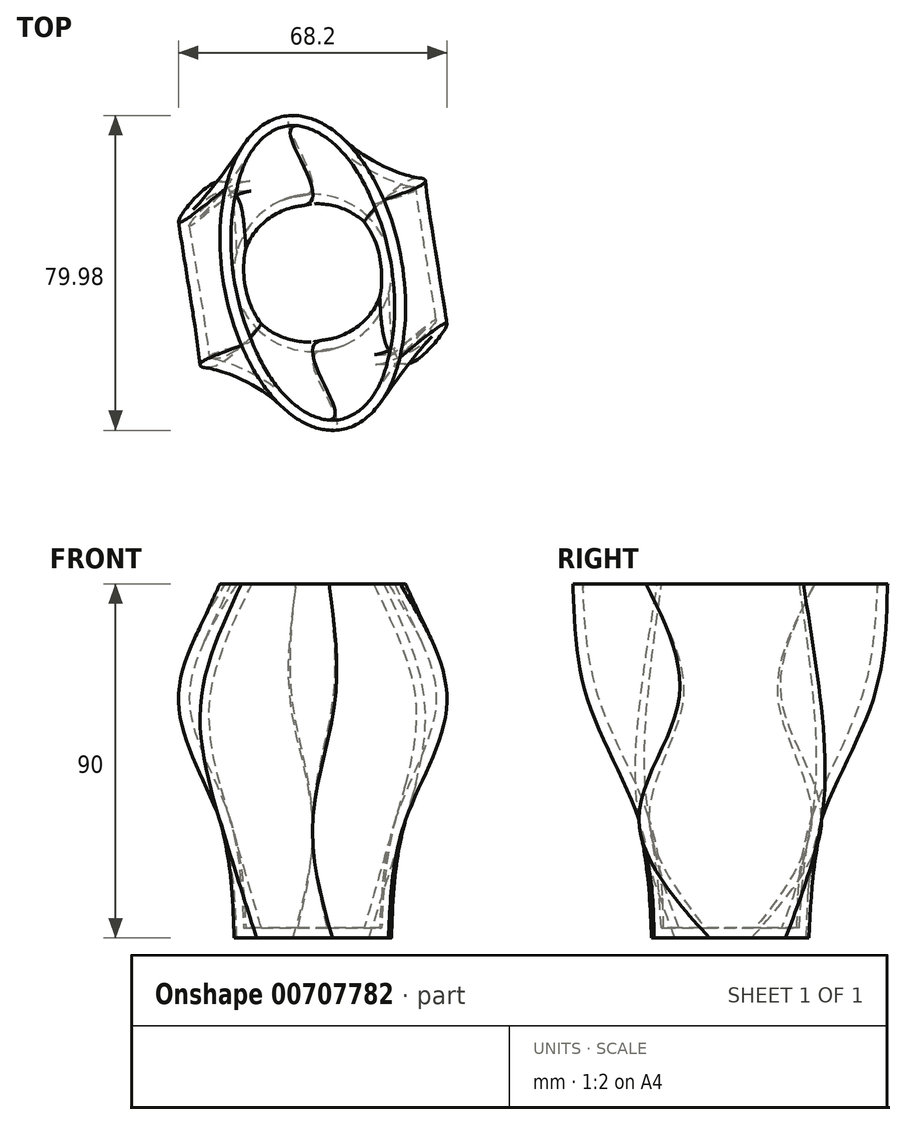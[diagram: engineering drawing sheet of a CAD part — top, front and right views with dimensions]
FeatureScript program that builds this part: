
annotation { "Feature Type Name" : "Feature", "Feature Type Description" : "" }
export const myFeature = defineFeature(function(context is Context, id is Id, definition is map)
    precondition{}
    {
        {
            var Q0;
            Q0=qCreatedBy(makeId("Top.planeOp"),FACE);
            cPlane(context, id + "F0", {"entities" : qUnion([Q0]), "cplaneType" : CPlaneType.OFFSET, "offset" : 30 * mm, "width" : 152.4 * mm, "height" : 152.4 * mm});
        }
        {
            var Q0;
            Q0=qCreatedBy(id+"F0.planeOp",FACE);
            cPlane(context, id + "F1", {"entities" : qUnion([Q0]), "cplaneType" : CPlaneType.OFFSET, "offset" : 30 * mm, "width" : 152.4 * mm, "height" : 152.4 * mm});
        }
        {
            var Q0;
            Q0=qCreatedBy(id+"F1.planeOp",FACE);
            cPlane(context, id + "F2", {"entities" : qUnion([Q0]), "cplaneType" : CPlaneType.OFFSET, "offset" : 30 * mm, "width" : 152.4 * mm, "height" : 152.4 * mm});
        }
        {
            var Q0;
            Q0=qCreatedBy(makeId("Top.planeOp"),FACE);
            var sketch = newSketch(context, id + "F3", { "sketchPlane" : qUnion([Q0])});
            skCircle(sketch, "E0", {"center": v(0, 0) * mm, "radius": 20 * mm});
            skSolve(sketch);
        }
        {
            var Q0;
            Q0=qCreatedBy(id+"F0.planeOp",FACE);
            var sketch = newSketch(context, id + "F4", { "sketchPlane" : qUnion([Q0])});
            skLineSegment(sketch, "E1.bottom", {"start": v(-23.6, -23.18) * mm, "end": v(23.6, -23.18) * mm});
            skLineSegment(sketch, "E1.top", {"start": v(-23.6, 23.18) * mm, "end": v(23.6, 23.18) * mm});
            skLineSegment(sketch, "E1.left", {"start": v(-23.6, -23.18) * mm, "end": v(-23.6, 23.18) * mm});
            skLineSegment(sketch, "E1.right", {"start": v(23.6, -23.18) * mm, "end": v(23.6, 23.18) * mm});
            skPoint(sketch, "E1.middle", {"position": v(0, 0) * mm});
            skSolve(sketch);
        }
        {
            var Q0;
            Q0=qCreatedBy(id+"F1.planeOp",FACE);
            var sketch = newSketch(context, id + "F5", { "sketchPlane" : qUnion([Q0])});
            skCircle(sketch, "E2.cCircle", {"center": v(0, 0) * mm, "radius": 31.65 * mm, "construction": true});
            skLineSegment(sketch, "E2.0", {"start": v(-28.44, -22.94) * mm, "end": v(-34.09, 13.16) * mm});
            skLineSegment(sketch, "E2.1", {"start": v(-34.09, 13.16) * mm, "end": v(-5.65, 36.1) * mm});
            skLineSegment(sketch, "E2.2", {"start": v(-5.65, 36.1) * mm, "end": v(28.44, 22.94) * mm});
            skLineSegment(sketch, "E2.3", {"start": v(28.44, 22.94) * mm, "end": v(34.09, -13.16) * mm});
            skLineSegment(sketch, "E2.4", {"start": v(34.09, -13.16) * mm, "end": v(5.65, -36.1) * mm});
            skLineSegment(sketch, "E2.5", {"start": v(5.65, -36.1) * mm, "end": v(-28.44, -22.94) * mm});
            skPoint(sketch, "E2.0.midPoint", {"position": v(-31.27, -4.9) * mm});
            skSolve(sketch);
        }
        {
            var Q0;
            Q0=qCreatedBy(id+"F2.planeOp",FACE);
            var sketch = newSketch(context, id + "F6", { "sketchPlane" : qUnion([Q0])});
            skEllipse(sketch, "E3", {"center": v(0, 0) * mm, "majorRadius": 40.46 * mm, "minorRadius": 22.76 * mm, "majorAxis": v(-0.18, 0.98)});
            skSolve(sketch);
        }
        {
            var Q0;
            Q0=makeQuery(id+"F3.imprint","IMPRINT",FACE,{"disambiguationData":[TD([[makeQuery(id+"F3.imprint","IMPRINT",EDGE,{"derivedFrom":sQuery(id+"F3.wireOp",EDGE,"E0")}),1.0]])]});
            var Q1;
            Q1=makeQuery(id+"F4.imprint","IMPRINT",FACE,{"disambiguationData":[TD([[makeQuery(id+"F4.imprint","IMPRINT",EDGE,{"derivedFrom":sQuery(id+"F4.wireOp",EDGE,"E1.bottom")}),1.0]])]});
            var Q2;
            Q2=makeQuery(id+"F5.imprint","IMPRINT",FACE,{"disambiguationData":[TD([[makeQuery(id+"F5.imprint","IMPRINT",EDGE,{"derivedFrom":sQuery(id+"F5.wireOp",EDGE,"E2.0")}),-1.0]])]});
            var Q3;
            Q3=makeQuery(id+"F6.imprint","IMPRINT",FACE,{"disambiguationData":[TD([[makeQuery(id+"F6.imprint","IMPRINT",EDGE,{"derivedFrom":sQuery(id+"F6.wireOp",EDGE,"E3")}),1.0]])]});
            loft(context, id + "F7", {"sheetProfilesArray" : [{ "sheetProfileEntities" : qUnion([Q0]) }, { "sheetProfileEntities" : qUnion([Q1]) }, { "sheetProfileEntities" : qUnion([Q2]) }, { "sheetProfileEntities" : qUnion([Q3]) }]});
        }
        {
            var Q0;
            Q0=makeQuery(id+"F7.opLoft","CAP_FACE",FACE,{"disambiguationData":[OSD([makeQuery(id+"F6.imprint","IMPRINT",FACE,{"disambiguationData":[TD([[makeQuery(id+"F6.imprint","IMPRINT",EDGE,{"derivedFrom":sQuery(id+"F6.wireOp",EDGE,"E3")}),1.0]])]})])],"isStart":true});
            shell(context, id + "F8", {"entities" : qUnion([Q0]), "thickness" : 2.54 * mm});
        }
    });
